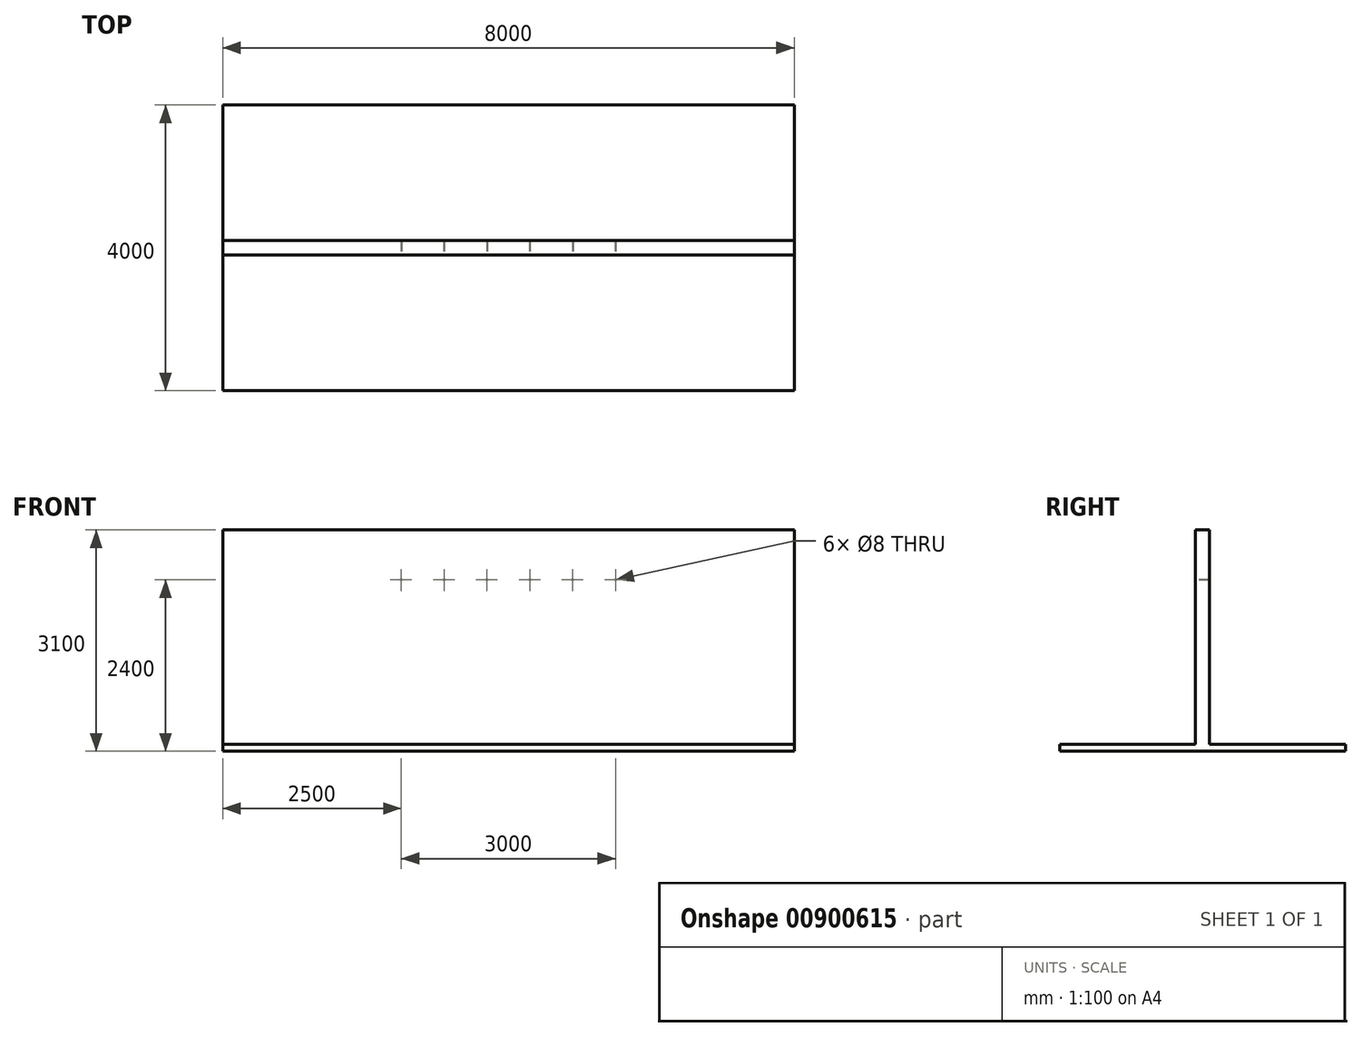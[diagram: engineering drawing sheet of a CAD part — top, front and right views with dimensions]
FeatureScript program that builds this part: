
annotation { "Feature Type Name" : "Feature", "Feature Type Description" : "" }
export const myFeature = defineFeature(function(context is Context, id is Id, definition is map)
    precondition{}
    {
        {
            var Q0;
            Q0=qCreatedBy(makeId("Top.planeOp"),FACE);
            var sketch = newSketch(context, id + "F0", { "sketchPlane" : qUnion([Q0])});
            skLineSegment(sketch, "E0.bottom", {"start": v(4000, -2000) * mm, "end": v(-4000, -2000) * mm});
            skLineSegment(sketch, "E0.top", {"start": v(4000, 2000) * mm, "end": v(-4000, 2000) * mm});
            skLineSegment(sketch, "E0.left", {"start": v(4000, -2000) * mm, "end": v(4000, 2000) * mm});
            skLineSegment(sketch, "E0.right", {"start": v(-4000, -2000) * mm, "end": v(-4000, 2000) * mm});
            skPoint(sketch, "E0.middle", {"position": v(0, 0) * mm});
            skSolve(sketch);
        }
        {
            var Q0;
            Q0=makeQuery(id+"F0.imprint","IMPRINT",FACE,{"disambiguationData":[TD([[makeQuery(id+"F0.imprint","IMPRINT",EDGE,{"derivedFrom":sQuery(id+"F0.wireOp",EDGE,"E0.bottom")}),-1.0]])]});
            extrude(context, id + "F1", {"entities" : qUnion([Q0]), "depth" : 100 * mm, "offsetDistance" : 25 * mm});
        }
        {
            var Q0;
            Q0=makeQuery(id+"F1.opExtrude","CAP_FACE",FACE,{"disambiguationData":[OSD([sQuery(id+"F0.wireOp",EDGE,"E0.bottom"),sQuery(id+"F0.wireOp",EDGE,"E0.top"),sQuery(id+"F0.wireOp",EDGE,"E0.left"),sQuery(id+"F0.wireOp",EDGE,"E0.right")])],"isStart":false});
            var sketch = newSketch(context, id + "F2", { "sketchPlane" : qUnion([Q0])});
            skLineSegment(sketch, "E1", {"start": v(-4000, 0) * mm, "end": v(-4000, 100) * mm});
            skLineSegment(sketch, "E2", {"start": v(-4000, 100) * mm, "end": v(4000, 100) * mm});
            skLineSegment(sketch, "E3", {"start": v(4000, 100) * mm, "end": v(4000, -100) * mm});
            skLineSegment(sketch, "E4", {"start": v(4000, -100) * mm, "end": v(-4000, -100) * mm});
            skLineSegment(sketch, "E5", {"start": v(-4000, -100) * mm, "end": v(-4000, 100) * mm});
            skSolve(sketch);
        }
        {
            var Q0;
            {var subQ0=sQuery(id+"F2.wireOp",EDGE,"E2");Q0=makeQuery(id+"F2.imprint","IMPRINT",FACE,{"disambiguationData":[TD([[makeQuery(id+"F2.imprint","IMPRINT",EDGE,{"derivedFrom":subQ0}),-1.0]])]});}
            extrude(context, id + "F3", {"entities" : qUnion([Q0]), "operationType" : NewBodyOperationType.ADD, "depth" : 3000 * mm, "offsetDistance" : 25 * mm});
        }
        {
            var Q0;
            Q0=makeQuery(id+"F3.opExtrude","SWEPT_FACE",FACE,{"disambiguationData":[OSD([sQuery(id+"F2.wireOp",EDGE,"E4")])]});
            var sketch = newSketch(context, id + "F4", { "sketchPlane" : qUnion([Q0])});
            skLineSegment(sketch, "E6", {"start": v(0, 0) * mm, "end": v(0, 3100) * mm});
            skLineSegment(sketch, "E7", {"start": v(-4000, 2400) * mm, "end": v(4000, 2400) * mm});
            skPoint(sketch, "E8", {"position": v(-1500, 2400) * mm});
            skPoint(sketch, "E9", {"position": v(-900, 2400) * mm});
            skPoint(sketch, "E10", {"position": v(-300, 2400) * mm});
            skPoint(sketch, "E11", {"position": v(300, 2400) * mm});
            skPoint(sketch, "E12", {"position": v(900, 2400) * mm});
            skPoint(sketch, "E13", {"position": v(1500, 2400) * mm});
            skSolve(sketch);
        }
        {
            var Q0;
            Q0=sQuery(id+"F4.wireOp",VERTEX,"E8");
            var Q1;
            Q1=sQuery(id+"F4.wireOp",VERTEX,"E9");
            var Q2;
            Q2=sQuery(id+"F4.wireOp",VERTEX,"E10");
            var Q3;
            Q3=sQuery(id+"F4.wireOp",VERTEX,"E11");
            var Q4;
            Q4=sQuery(id+"F4.wireOp",VERTEX,"E12");
            var Q5;
            Q5=sQuery(id+"F4.wireOp",VERTEX,"E13");
            var Q6;
            Q6=makeQuery(id+"F1.opExtrude","SWEPT_BODY",BODY,{"disambiguationData":[OSD([sQuery(id+"F0.wireOp",EDGE,"E0.bottom"),sQuery(id+"F0.wireOp",EDGE,"E0.top"),sQuery(id+"F0.wireOp",EDGE,"E0.left"),sQuery(id+"F0.wireOp",EDGE,"E0.right")])]});
            hole(context, id + "F5", {"style" : HoleStyle.SIMPLE, "endStyle" : HoleEndStyle.THROUGH, "holeDiameter" : 8 * mm, "majorDiameter" : 5 * mm, "isTappedThrough" : true, "tappedDepth" : 12 * mm, "tapClearance" : 3, "locations" : qUnion([Q0, Q1, Q2, Q3, Q4, Q5]), "scope" : qUnion([Q6])});
        }
    });
